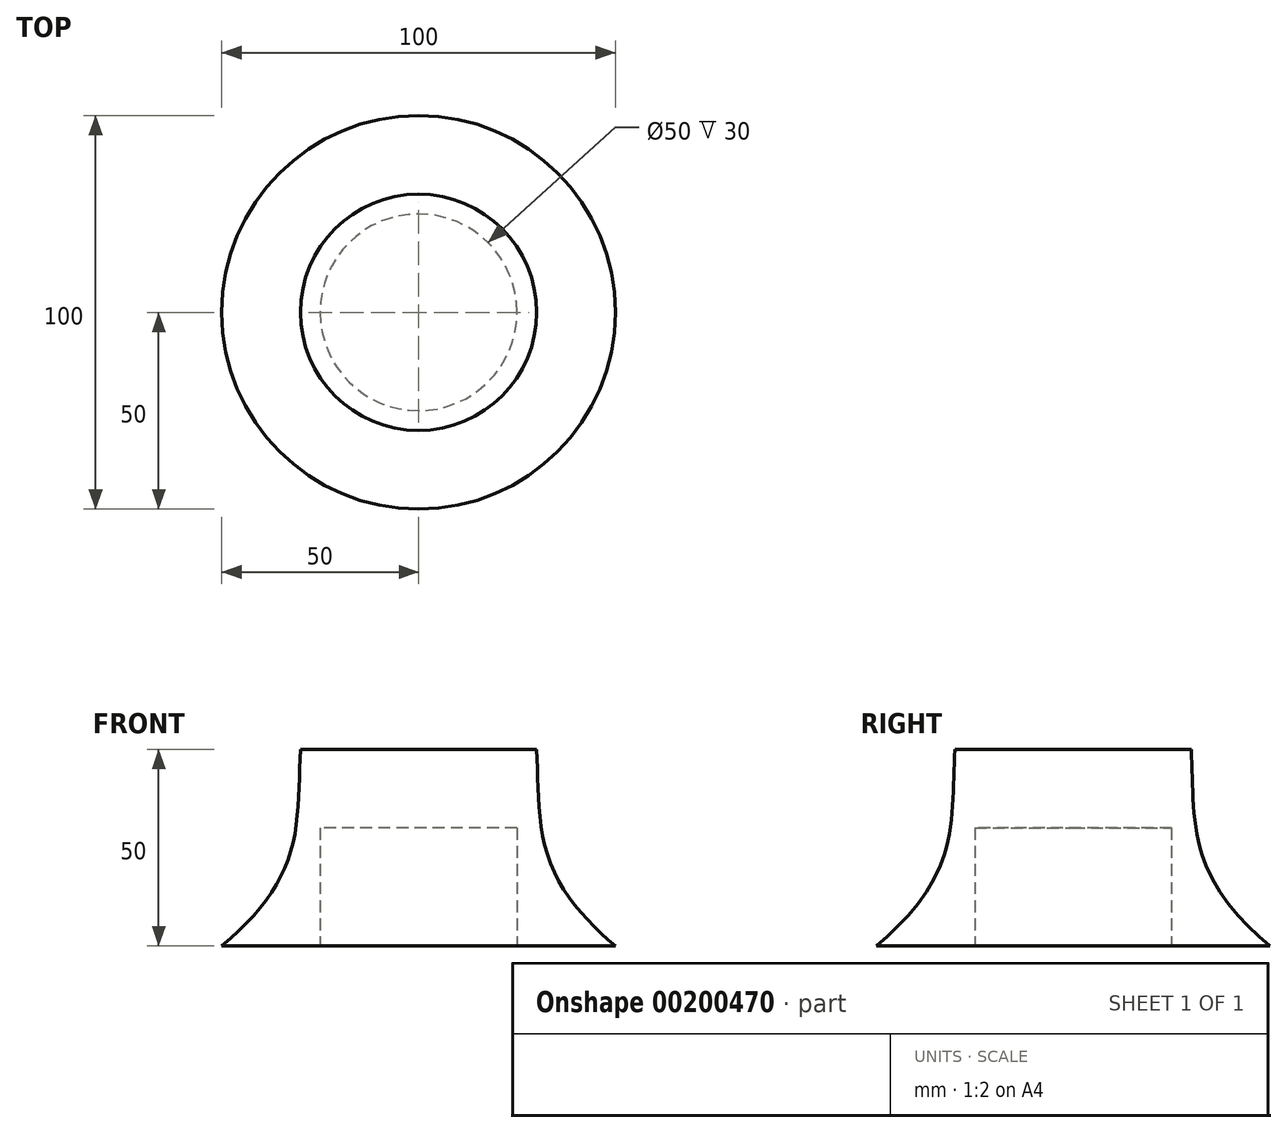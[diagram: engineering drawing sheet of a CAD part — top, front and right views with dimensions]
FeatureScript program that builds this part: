
annotation { "Feature Type Name" : "Feature", "Feature Type Description" : "" }
export const myFeature = defineFeature(function(context is Context, id is Id, definition is map)
    precondition{}
    {
        {
            var Q0;
            Q0=qCreatedBy(makeId("Front.planeOp"),FACE);
            var sketch = newSketch(context, id + "F0", { "sketchPlane" : qUnion([Q0])});
            skLineSegment(sketch, "E0", {"start": v(0, 0) * mm, "end": v(0, 50) * mm});
            skLineSegment(sketch, "E1", {"start": v(0, 0) * mm, "end": v(-50, 0) * mm});
            skLineSegment(sketch, "E2", {"start": v(0, 50) * mm, "end": v(-30, 50) * mm});
            skFitSpline(sketch, "E3", {"points": [v(-30, 50) * mm, v(-32.62, 23.53) * mm, v(-50, 0) * mm], "startDerivative": vector(-2.95, -56.23) * mm, "endDerivative": vector(-52.41, -44.05) * mm});
            skSolve(sketch);
        }
        {
            var Q0;
            Q0 = qSketchRegion(id + "F0", true);
            var Q1;
            Q1=sQuery(id+"F0.wireOp",EDGE,"E0");
            revolve(context, id + "F1", {"entities" : qUnion([Q0]), "axis" : qUnion([Q1]), "revolveType" : RevolveType.FULL});
        }
        {
            var Q0;
            Q0=qCreatedBy(makeId("Top.planeOp"),FACE);
            var sketch = newSketch(context, id + "F2", { "sketchPlane" : qUnion([Q0])});
            skCircle(sketch, "E4", {"center": v(0, 0) * mm, "radius": 25 * mm});
            skSolve(sketch);
        }
        {
            var Q0;
            Q0 = qSketchRegion(id + "F2", true);
            extrude(context, id + "F3", {"entities" : qUnion([Q0]), "operationType" : NewBodyOperationType.REMOVE, "depth" : 30 * mm});
        }
    });
